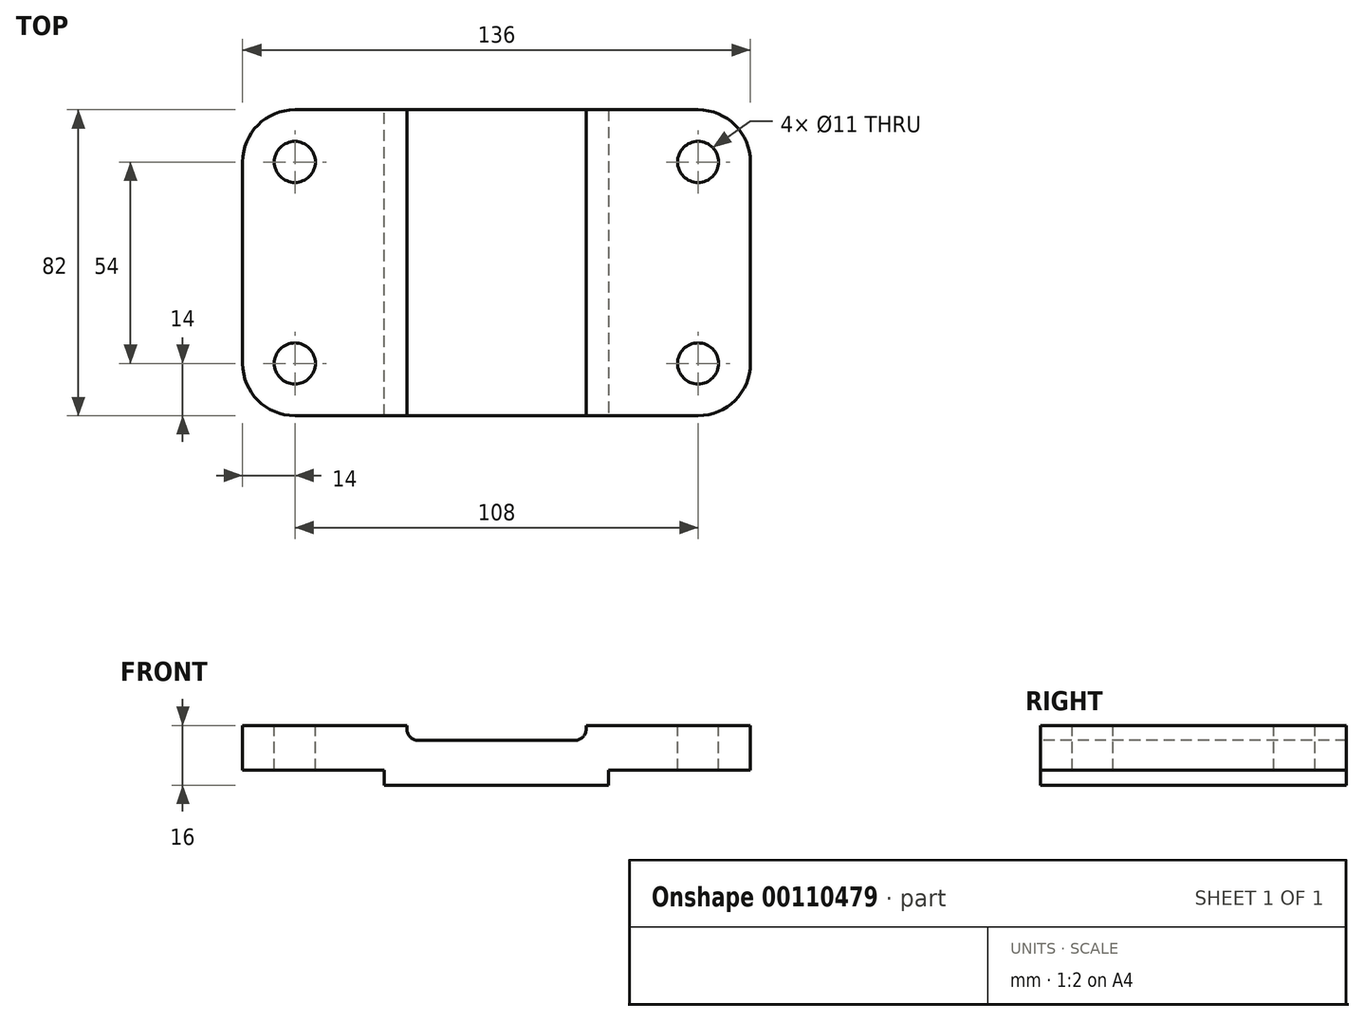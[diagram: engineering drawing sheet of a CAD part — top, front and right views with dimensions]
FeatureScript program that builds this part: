
annotation { "Feature Type Name" : "Feature", "Feature Type Description" : "" }
export const myFeature = defineFeature(function(context is Context, id is Id, definition is map)
    precondition{}
    {
        {
            var Q0;
            Q0=qCreatedBy(makeId("Top.planeOp"),FACE);
            var sketch = newSketch(context, id + "F0", { "sketchPlane" : qUnion([Q0])});
            skLineSegment(sketch, "E0.bottom", {"start": v(54, 41) * mm, "end": v(-54, 41) * mm});
            skLineSegment(sketch, "E0.top", {"start": v(54, -41) * mm, "end": v(-54, -41) * mm});
            skLineSegment(sketch, "E0.left", {"start": v(68, 27) * mm, "end": v(68, -27) * mm});
            skLineSegment(sketch, "E0.right", {"start": v(-68, 27) * mm, "end": v(-68, -27) * mm});
            skPoint(sketch, "E0.middle", {"position": v(0, 0) * mm});
            skPoint(sketch, "E1.visualSharp", {"position": v(68, 41) * mm});
            skArc(sketch, "E1.filletArc", {"start": v(68, 27) * mm, "mid": v(63.9, 36.9) * mm, "end": v(54, 41) * mm});
            skPoint(sketch, "E2.visualSharp", {"position": v(68, -41) * mm});
            skArc(sketch, "E2.filletArc", {"start": v(54, -41) * mm, "mid": v(63.9, -36.9) * mm, "end": v(68, -27) * mm});
            skPoint(sketch, "E3.visualSharp", {"position": v(-68, 41) * mm});
            skArc(sketch, "E3.filletArc", {"start": v(-54, 41) * mm, "mid": v(-63.9, 36.9) * mm, "end": v(-68, 27) * mm});
            skPoint(sketch, "E4.visualSharp", {"position": v(-68, -41) * mm});
            skArc(sketch, "E4.filletArc", {"start": v(-68, -27) * mm, "mid": v(-63.9, -36.9) * mm, "end": v(-54, -41) * mm});
            skSolve(sketch);
        }
        {
            var Q0;
            Q0 = qSketchRegion(id + "F0", true);
            extrude(context, id + "F1", {"entities" : qUnion([Q0]), "depth" : 12 * mm});
        }
        {
            var Q0;
            Q0=makeQuery(id+"F1.opExtrude","CAP_FACE",FACE,{"disambiguationData":[OSD([sQuery(id+"F0.wireOp",EDGE,"E0.bottom"),sQuery(id+"F0.wireOp",EDGE,"E0.top"),sQuery(id+"F0.wireOp",EDGE,"E0.left"),sQuery(id+"F0.wireOp",EDGE,"E0.right"),sQuery(id+"F0.wireOp",EDGE,"E1.filletArc"),sQuery(id+"F0.wireOp",EDGE,"E2.filletArc"),sQuery(id+"F0.wireOp",EDGE,"E3.filletArc"),sQuery(id+"F0.wireOp",EDGE,"E4.filletArc")])],"isStart":false});
            var sketch = newSketch(context, id + "F2", { "sketchPlane" : qUnion([Q0])});
            skLineSegment(sketch, "E5", {"start": v(-24, 41) * mm, "end": v(-24, -41) * mm});
            skLineSegment(sketch, "E6", {"start": v(24, 41) * mm, "end": v(24, -41) * mm});
            skSolve(sketch);
        }
        {
            var Q0;
            Q0 = qSketchRegion(id + "F2", true);
            var Q1;
            {var subQ0=sQuery(id+"F2.wireOp",EDGE,"E5");Q1=makeQuery(id+"F2.imprint","IMPRINT",FACE,{"disambiguationData":[TD([[makeQuery(id+"F2.imprint","IMPRINT",EDGE,{"derivedFrom":subQ0}),1.0]])]});}
            extrude(context, id + "F3", {"entities" : qUnion([Q0, Q1]), "operationType" : NewBodyOperationType.REMOVE, "oppositeDirection" : true, "depth" : 4 * mm});
        }
        {
            var Q0;
            Q0=makeQuery(id+"F3.boolean.opBoolean","COPY",EDGE,{"derivedFrom":makeQuery(id+"F3.opExtrude","CAP_EDGE",EDGE,{"disambiguationData":[OSD([sQuery(id+"F2.wireOp",EDGE,"E5")])],"isStart":false})});
            var Q1;
            Q1=makeQuery(id+"F3.boolean.opBoolean","COPY",EDGE,{"derivedFrom":makeQuery(id+"F3.opExtrude","CAP_EDGE",EDGE,{"disambiguationData":[OSD([sQuery(id+"F2.wireOp",EDGE,"E6")])],"isStart":false})});
            fillet(context, id + "F4", {"entities" : qUnion([Q0, Q1]), "radius" : 3 * mm, "tangentPropagation" : true, "allowEdgeOverflow" : false});
        }
        {
            var Q0;
            Q0=makeQuery(id+"F1.opExtrude","CAP_FACE",FACE,{"disambiguationData":[OSD([sQuery(id+"F0.wireOp",EDGE,"E0.bottom"),sQuery(id+"F0.wireOp",EDGE,"E0.top"),sQuery(id+"F0.wireOp",EDGE,"E0.left"),sQuery(id+"F0.wireOp",EDGE,"E0.right"),sQuery(id+"F0.wireOp",EDGE,"E1.filletArc"),sQuery(id+"F0.wireOp",EDGE,"E2.filletArc"),sQuery(id+"F0.wireOp",EDGE,"E3.filletArc"),sQuery(id+"F0.wireOp",EDGE,"E4.filletArc")])],"isStart":true});
            var sketch = newSketch(context, id + "F5", { "sketchPlane" : qUnion([Q0])});
            skLineSegment(sketch, "E7", {"start": v(-30, 41) * mm, "end": v(-30, -41) * mm});
            skLineSegment(sketch, "E8", {"start": v(30, -41) * mm, "end": v(30, 41) * mm});
            skSolve(sketch);
        }
        {
            var Q0;
            Q0 = qSketchRegion(id + "F5", true);
            var Q1;
            {var subQ0=sQuery(id+"F5.wireOp",EDGE,"E7");Q1=makeQuery(id+"F5.imprint","IMPRINT",FACE,{"disambiguationData":[TD([[makeQuery(id+"F5.imprint","IMPRINT",EDGE,{"derivedFrom":subQ0}),1.0]])]});}
            extrude(context, id + "F6", {"entities" : qUnion([Q0, Q1]), "operationType" : NewBodyOperationType.ADD, "depth" : 4 * mm});
        }
        {
            var Q0;
            {var subQ0=sQuery(id+"F0.wireOp",EDGE,"E0.right");var subQ1=sQuery(id+"F0.wireOp",EDGE,"E3.filletArc");var subQ2=sQuery(id+"F0.wireOp",EDGE,"E0.top");var subQ3=sQuery(id+"F0.wireOp",EDGE,"E0.bottom");var subQ4=sQuery(id+"F0.wireOp",EDGE,"E4.filletArc");Q0=makeQuery(id+"F3.boolean.opBoolean","SPLIT",FACE,{"disambiguationData":[TD([makeQuery(id+"F1.opExtrude","SWEPT_FACE",FACE,{"disambiguationData":[OSD([subQ0])]})])],"derivedFrom":makeQuery(id+"F1.opExtrude","CAP_FACE",FACE,{"disambiguationData":[OSD([subQ3,subQ2,sQuery(id+"F0.wireOp",EDGE,"E0.left"),subQ0,sQuery(id+"F0.wireOp",EDGE,"E1.filletArc"),sQuery(id+"F0.wireOp",EDGE,"E2.filletArc"),subQ1,subQ4])],"isStart":false})});}
            var sketch = newSketch(context, id + "F7", { "sketchPlane" : qUnion([Q0])});
            skLineSegment(sketch, "E9", {"start": v(-76.22, 27) * mm, "end": v(85.9, 27) * mm, "construction": true});
            skLineSegment(sketch, "E10", {"start": v(85.9, 27) * mm, "end": v(87.64, 27) * mm, "construction": true});
            skLineSegment(sketch, "E11", {"start": v(-76.22, -27) * mm, "end": v(90.62, -27) * mm, "construction": true});
            skLineSegment(sketch, "E12", {"start": v(54, -53.14) * mm, "end": v(54, 60.32) * mm, "construction": true});
            skLineSegment(sketch, "E13", {"start": v(-54, 61.81) * mm, "end": v(-54, -53.39) * mm, "construction": true});
            skCircle(sketch, "E14", {"center": v(-54, 27) * mm, "radius": 5.5 * mm});
            skCircle(sketch, "E15.MirrorC", {"center": v(-54, -27) * mm, "radius": 5.5 * mm});
            skCircle(sketch, "E16.MirrorC", {"center": v(54, -27) * mm, "radius": 5.5 * mm});
            skCircle(sketch, "E17.MirrorC", {"center": v(54, 27) * mm, "radius": 5.5 * mm});
            skSolve(sketch);
        }
        {
            var Q0;
            Q0 = qSketchRegion(id + "F7", true);
            extrude(context, id + "F8", {"entities" : qUnion([Q0]), "operationType" : NewBodyOperationType.REMOVE, "endBound" : BoundingType.THROUGH_ALL, "oppositeDirection" : true, "depth" : 25 * mm});
        }
    });
